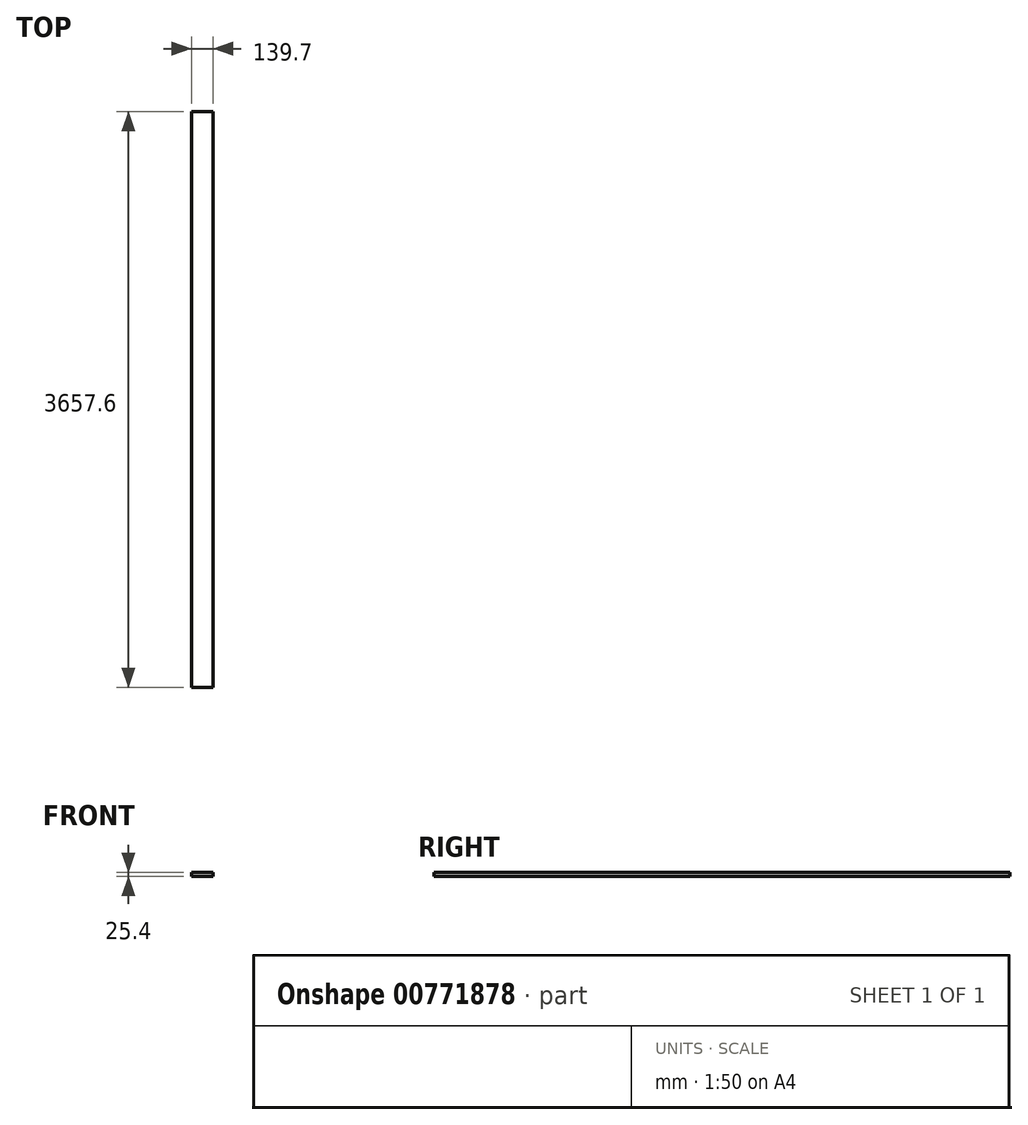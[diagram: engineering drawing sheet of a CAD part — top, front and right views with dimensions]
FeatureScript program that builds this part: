
annotation { "Feature Type Name" : "Feature", "Feature Type Description" : "" }
export const myFeature = defineFeature(function(context is Context, id is Id, definition is map)
    precondition{}
    {
        {
            var Q0;
            Q0=qCreatedBy(makeId("Front.planeOp"),FACE);
            var sketch = newSketch(context, id + "F0", { "sketchPlane" : qUnion([Q0])});
            skLineSegment(sketch, "E0.bottom", {"start": v(69.85, 12.7) * mm, "end": v(-69.85, 12.7) * mm});
            skLineSegment(sketch, "E0.top", {"start": v(69.85, -12.7) * mm, "end": v(-69.85, -12.7) * mm});
            skLineSegment(sketch, "E0.left", {"start": v(69.85, 12.7) * mm, "end": v(69.85, -12.7) * mm});
            skLineSegment(sketch, "E0.right", {"start": v(-69.85, 12.7) * mm, "end": v(-69.85, -12.7) * mm});
            skPoint(sketch, "E0.middle", {"position": v(0, 0) * mm});
            skSolve(sketch);
        }
        {
            var Q0;
            Q0 = qSketchRegion(id + "F0", true);
            extrude(context, id + "F1", {"entities" : qUnion([Q0]), "depth" : 3657.6 * mm, "offsetDistance" : 25.4 * mm});
        }
    });
